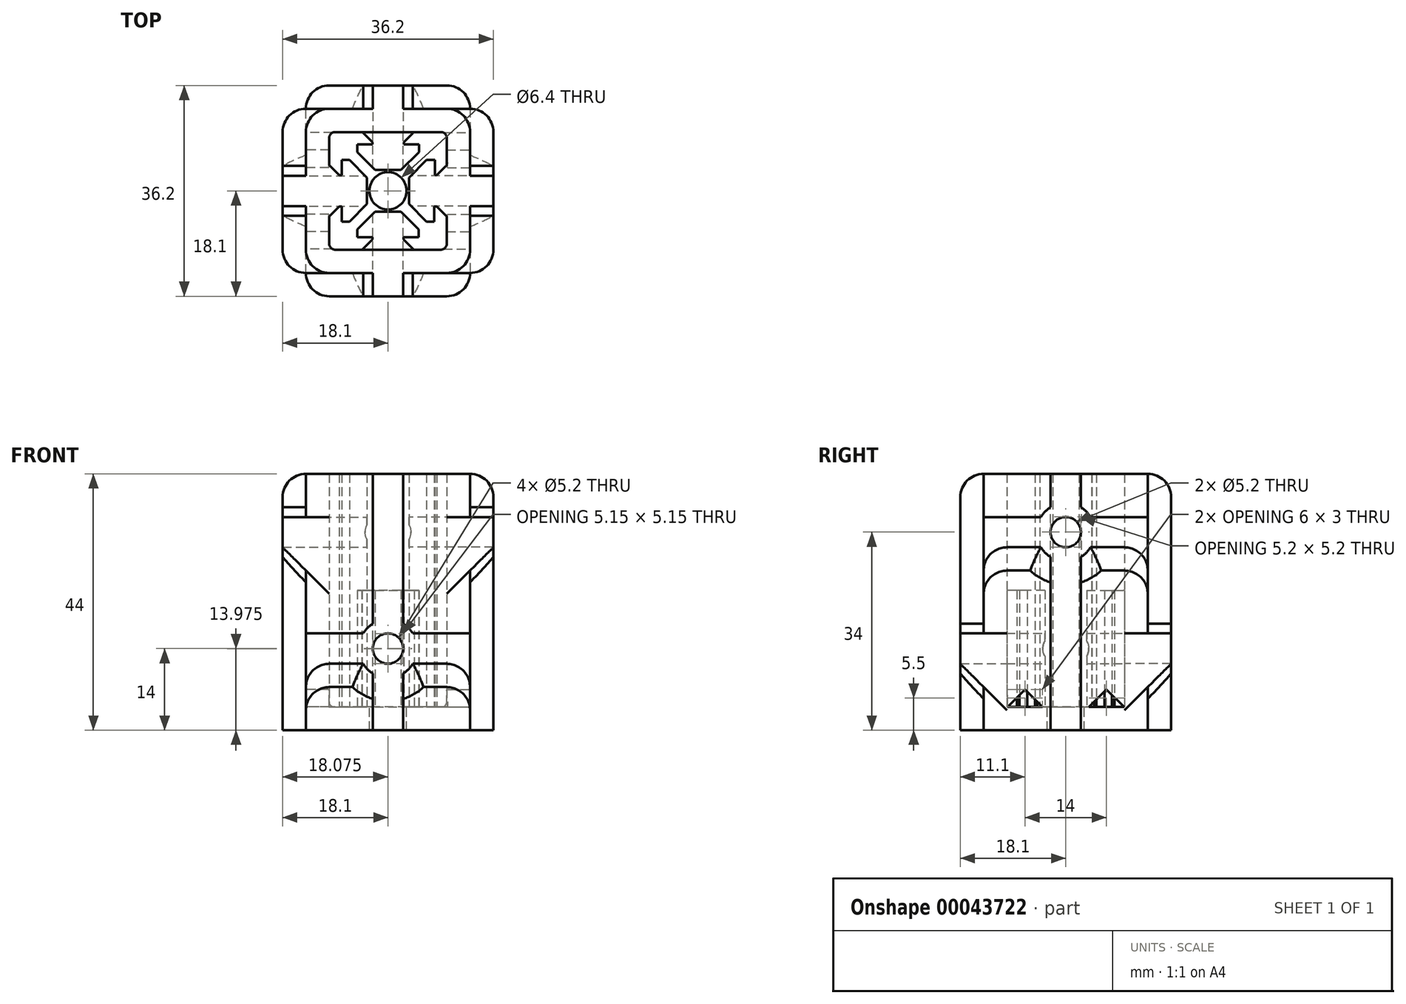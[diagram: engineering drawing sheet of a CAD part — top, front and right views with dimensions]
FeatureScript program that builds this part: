
annotation { "Feature Type Name" : "Feature", "Feature Type Description" : "" }
export const myFeature = defineFeature(function(context is Context, id is Id, definition is map)
    precondition{}
    {
        {
            var Q0;
            Q0=qCreatedBy(makeId("Top.planeOp"),FACE);
            var sketch = newSketch(context, id + "F0", { "sketchPlane" : qUnion([Q0])});
            skLineSegment(sketch, "E0.rect.bottom", {"start": v(10.1, -10.1) * mm, "end": v(-10.1, -10.1) * mm});
            skLineSegment(sketch, "E0.rect.top", {"start": v(10.1, 10.1) * mm, "end": v(-10.1, 10.1) * mm, "construction": true});
            skLineSegment(sketch, "E0.rect.left", {"start": v(10.1, -10.1) * mm, "end": v(10.1, 10.1) * mm, "construction": true});
            skLineSegment(sketch, "E0.rect.right", {"start": v(-10.1, -10.1) * mm, "end": v(-10.1, 10.1) * mm});
            skPoint(sketch, "E0.rect.middle", {"position": v(0, 0) * mm});
            skLineSegment(sketch, "E1.0", {"start": v(14.1, -14.1) * mm, "end": v(14.1, 14.1) * mm, "construction": true});
            skLineSegment(sketch, "E1.1", {"start": v(14.1, -14.1) * mm, "end": v(-14.1, -14.1) * mm});
            skLineSegment(sketch, "E1.2", {"start": v(-14.1, -14.1) * mm, "end": v(-14.1, 14.1) * mm});
            skLineSegment(sketch, "E1.3", {"start": v(14.1, 14.1) * mm, "end": v(-14.1, 14.1) * mm, "construction": true});
            skCircle(sketch, "E2", {"center": v(0, 0) * mm, "radius": 3.2 * mm});
            skLineSegment(sketch, "E3", {"start": v(-14.1, 14.1) * mm, "end": v(-2.26, 2.26) * mm});
            skLineSegment(sketch, "E4", {"start": v(2.26, -2.26) * mm, "end": v(14.1, -14.1) * mm});
            skSolve(sketch);
        }
        {
            var Q0;
            {var subQ5=sQuery(id+"F0.wireOp",EDGE,"E0.rect.right");Q0=makeQuery(id+"F0.imprint","IMPRINT",FACE,{"disambiguationData":[TD([[makeQuery(id+"F0.imprint","IMPRINT",EDGE,{"derivedFrom":subQ5}),1.0]])]});}
            extrude(context, id + "F1", {"entities" : qUnion([Q0]), "depth" : 40 * mm});
        }
        {
            var Q0;
            {var subQ3=sQuery(id+"F0.wireOp",EDGE,"E0.rect.bottom");Q0=makeQuery(id+"F0.imprint","IMPRINT",FACE,{"disambiguationData":[TD([[makeQuery(id+"F0.imprint","IMPRINT",EDGE,{"derivedFrom":subQ3}),1.0]])]});}
            var Q1;
            {var subQ0=sQuery(id+"F0.wireOp",EDGE,"E0.rect.bottom");Q1=makeQuery(id+"F0.imprint","IMPRINT",FACE,{"disambiguationData":[TD([[makeQuery(id+"F0.imprint","IMPRINT",EDGE,{"derivedFrom":subQ0}),-1.0]])]});}
            extrude(context, id + "F2", {"entities" : qUnion([Q0, Q1]), "operationType" : NewBodyOperationType.ADD, "oppositeDirection" : true, "depth" : 4 * mm});
        }
        {
            var Q0;
            Q0=qCreatedBy(makeId("Front.planeOp"),FACE);
            var sketch = newSketch(context, id + "F3", { "sketchPlane" : qUnion([Q0])});
            skCircle(sketch, "E5", {"center": v(0, 10) * mm, "radius": 2.6 * mm});
            skSolve(sketch);
        }
        {
            var Q0;
            Q0=makeQuery(id+"F3.imprint","IMPRINT",FACE,{"disambiguationData":[TD([[makeQuery(id+"F3.imprint","IMPRINT",EDGE,{"derivedFrom":sQuery(id+"F3.wireOp",EDGE,"E5")}),1.0]])]});
            extrude(context, id + "F4", {"entities" : qUnion([Q0]), "operationType" : NewBodyOperationType.REMOVE, "depth" : 25 * mm});
        }
        {
            var Q0;
            Q0=makeQuery(id+"F3.imprint","IMPRINT",FACE,{"disambiguationData":[TD([[makeQuery(id+"F3.imprint","IMPRINT",EDGE,{"derivedFrom":sQuery(id+"F3.wireOp",EDGE,"E5")}),-1.0]])]});
            var Q1;
            Q1=makeQuery(id+"F3.imprint","IMPRINT",FACE,{"disambiguationData":[TD([[makeQuery(id+"F3.imprint","IMPRINT",EDGE,{"derivedFrom":sQuery(id+"F3.wireOp",EDGE,"E5")}),1.0]])]});
            extrude(context, id + "F5", {"entities" : qUnion([Q0, Q1]), "operationType" : NewBodyOperationType.REMOVE, "oppositeDirection" : true, "depth" : 25 * mm});
        }
        {
            var Q0;
            Q0=qCreatedBy(makeId("Right.planeOp"),FACE);
            var sketch = newSketch(context, id + "F6", { "sketchPlane" : qUnion([Q0])});
            skCircle(sketch, "E6", {"center": v(0, 30) * mm, "radius": 2.6 * mm});
            skLineSegment(sketch, "E7", {"start": v(-10, 0) * mm, "end": v(-4, 0) * mm});
            skLineSegment(sketch, "E8", {"start": v(-4, 0) * mm, "end": v(-7, 3) * mm});
            skLineSegment(sketch, "E9", {"start": v(-7, 3) * mm, "end": v(-10, 0) * mm});
            skLineSegment(sketch, "E10", {"start": v(0, 0) * mm, "end": v(0, 30) * mm, "construction": true});
            skLineSegment(sketch, "E11.MirrorCS", {"start": v(10, 0) * mm, "end": v(4, 0) * mm});
            skLineSegment(sketch, "E12.MirrorCS", {"start": v(4, 0) * mm, "end": v(7, 3) * mm});
            skLineSegment(sketch, "E13.MirrorCS", {"start": v(7, 3) * mm, "end": v(10, 0) * mm});
            skSolve(sketch);
        }
        {
            var Q0;
            Q0=makeQuery(id+"F6.imprint","IMPRINT",FACE,{"disambiguationData":[TD([[makeQuery(id+"F6.imprint","IMPRINT",EDGE,{"derivedFrom":sQuery(id+"F6.wireOp",EDGE,"E6")}),1.0]])]});
            var Q1;
            Q1=makeQuery(id+"F6.imprint","IMPRINT",FACE,{"disambiguationData":[TD([[makeQuery(id+"F6.imprint","IMPRINT",EDGE,{"derivedFrom":sQuery(id+"F6.wireOp",EDGE,"f3287db6-100c-4814-bab7-777f2fd4f9ab")}),1.0]])]});
            extrude(context, id + "F7", {"entities" : qUnion([Q0, Q1]), "operationType" : NewBodyOperationType.REMOVE, "endBound" : BoundingType.SYMMETRIC, "oppositeDirection" : true, "depth" : 50 * mm});
        }
        {
            var Q0;
            Q0=makeQuery(id+"F6.imprint","IMPRINT",FACE,{"disambiguationData":[TD([[makeQuery(id+"F6.imprint","IMPRINT",EDGE,{"derivedFrom":sQuery(id+"F6.wireOp",EDGE,"E11.MirrorCS")}),-1.0]])]});
            var Q1;
            Q1=makeQuery(id+"F6.imprint","IMPRINT",FACE,{"disambiguationData":[TD([[makeQuery(id+"F6.imprint","IMPRINT",EDGE,{"derivedFrom":sQuery(id+"F6.wireOp",EDGE,"E7")}),1.0]])]});
            extrude(context, id + "F8", {"entities" : qUnion([Q0, Q1]), "operationType" : NewBodyOperationType.REMOVE, "endBound" : BoundingType.SYMMETRIC, "depth" : 50 * mm});
        }
        {
            var Q0;
            {var subQ0=sQuery(id+"F0.wireOp",EDGE,"E1.1");Q0=makeQuery(id+"F2.boolean.opBoolean","MERGE",FACE,{"derivedFrom":[makeQuery(id+"F9Dm1DlvACU9APN_1.boolean.opBoolean","MERGE",FACE,{"derivedFrom":[makeQuery(id+"F1.opExtrude","SWEPT_FACE",FACE,{"disambiguationData":[OSD([subQ0])]}),makeQuery(id+"F9Dm1DlvACU9APN_1.opExtrude","SWEPT_FACE",FACE,{"disambiguationData":[OSD([subQ0])]})]}),makeQuery(id+"F2.opExtrude","SWEPT_FACE",FACE,{"disambiguationData":[OSD([subQ0])]})]});}
            var sketch = newSketch(context, id + "F9", { "sketchPlane" : qUnion([Q0])});
            skArc(sketch, "E14", {"start": v(-4.27, 7.4) * mm, "mid": v(-3.54, 6.46) * mm, "end": v(-2.6, 5.73) * mm});
            skLineSegment(sketch, "E15.rect.bottom", {"start": v(2.6, 40) * mm, "end": v(-2.6, 40) * mm});
            skLineSegment(sketch, "E15.rect.left", {"start": v(2.6, 40) * mm, "end": v(2.6, 14.27) * mm});
            skLineSegment(sketch, "E15.rect.right", {"start": v(-2.6, 40) * mm, "end": v(-2.6, 14.27) * mm});
            skLineSegment(sketch, "E16.rect.bottom", {"start": v(14.1, 12.6) * mm, "end": v(4.27, 12.6) * mm});
            skLineSegment(sketch, "E16.rect.top", {"start": v(14.1, 7.4) * mm, "end": v(4.27, 7.4) * mm});
            skLineSegment(sketch, "E16.rect.left", {"start": v(14.1, 12.6) * mm, "end": v(14.1, 7.4) * mm});
            skLineSegment(sketch, "E16.rect.right", {"start": v(-14.1, 12.6) * mm, "end": v(-14.1, 7.4) * mm});
            skLineSegment(sketch, "E17.0", {"start": v(2.6, -4) * mm, "end": v(-2.6, -4) * mm});
            skLineSegment(sketch, "E18.trimOffspring", {"start": v(-2.6, 5.73) * mm, "end": v(-2.6, -4) * mm});
            skLineSegment(sketch, "E19.trimOffspring", {"start": v(-4.27, 7.4) * mm, "end": v(-14.1, 7.4) * mm});
            skLineSegment(sketch, "E20.trimOffspring", {"start": v(-4.27, 12.6) * mm, "end": v(-14.1, 12.6) * mm});
            skLineSegment(sketch, "E21.trimOffspring", {"start": v(2.6, 5.73) * mm, "end": v(2.6, -4) * mm});
            skArc(sketch, "E22.trimOffspring", {"start": v(-2.6, 14.27) * mm, "mid": v(-3.54, 13.54) * mm, "end": v(-4.27, 12.6) * mm});
            skArc(sketch, "E23.trimOffspring", {"start": v(4.27, 12.6) * mm, "mid": v(3.54, 13.54) * mm, "end": v(2.6, 14.27) * mm});
            skArc(sketch, "E24.trimOffspring", {"start": v(2.6, 5.73) * mm, "mid": v(3.54, 6.46) * mm, "end": v(4.27, 7.4) * mm});
            skSolve(sketch);
        }
        {
            var Q0;
            {var subQ0=sQuery(id+"F0.wireOp",EDGE,"E1.2");Q0=makeQuery(id+"F2.boolean.opBoolean","MERGE",FACE,{"derivedFrom":[makeQuery(id+"F1.opExtrude","SWEPT_FACE",FACE,{"disambiguationData":[OSD([subQ0])]}),makeQuery(id+"F2.opExtrude","SWEPT_FACE",FACE,{"disambiguationData":[OSD([subQ0])]})]});}
            var sketch = newSketch(context, id + "F10", { "sketchPlane" : qUnion([Q0])});
            skArc(sketch, "E25", {"start": v(-4.27, 27.4) * mm, "mid": v(-3.54, 26.46) * mm, "end": v(-2.6, 25.73) * mm});
            skLineSegment(sketch, "E26.rect.bottom", {"start": v(2.6, -4) * mm, "end": v(-2.6, -4) * mm});
            skLineSegment(sketch, "E26.rect.left", {"start": v(2.6, -4) * mm, "end": v(2.6, 25.73) * mm});
            skLineSegment(sketch, "E26.rect.right", {"start": v(-2.6, -4) * mm, "end": v(-2.6, 25.73) * mm});
            skLineSegment(sketch, "E27.0", {"start": v(2.6, 40) * mm, "end": v(-2.6, 40) * mm});
            skLineSegment(sketch, "E28.rect.bottom", {"start": v(14.1, 32.6) * mm, "end": v(4.27, 32.6) * mm});
            skLineSegment(sketch, "E28.rect.top", {"start": v(14.1, 27.4) * mm, "end": v(4.27, 27.4) * mm});
            skLineSegment(sketch, "E28.rect.left", {"start": v(14.1, 32.6) * mm, "end": v(14.1, 27.4) * mm});
            skLineSegment(sketch, "E28.rect.right", {"start": v(-14.1, 32.6) * mm, "end": v(-14.1, 27.4) * mm});
            skLineSegment(sketch, "E29.trimOffspring", {"start": v(-4.27, 32.6) * mm, "end": v(-14.1, 32.6) * mm});
            skLineSegment(sketch, "E30.trimOffspring", {"start": v(-2.6, 34.27) * mm, "end": v(-2.6, 40) * mm});
            skLineSegment(sketch, "E31.trimOffspring", {"start": v(2.6, 34.27) * mm, "end": v(2.6, 40) * mm});
            skLineSegment(sketch, "E32.trimOffspring", {"start": v(-4.27, 27.4) * mm, "end": v(-14.1, 27.4) * mm});
            skArc(sketch, "E33.trimOffspring", {"start": v(-2.6, 34.27) * mm, "mid": v(-3.54, 33.54) * mm, "end": v(-4.27, 32.6) * mm});
            skArc(sketch, "E34.trimOffspring", {"start": v(4.27, 32.6) * mm, "mid": v(3.54, 33.54) * mm, "end": v(2.6, 34.27) * mm});
            skArc(sketch, "E35.trimOffspring", {"start": v(2.6, 25.73) * mm, "mid": v(3.54, 26.46) * mm, "end": v(4.27, 27.4) * mm});
            skSolve(sketch);
        }
        {
            var Q0;
            Q0=makeQuery(id+"F9.imprint","IMPRINT",FACE,{"disambiguationData":[TD([[makeQuery(id+"F9.imprint","IMPRINT",EDGE,{"derivedFrom":sQuery(id+"F9.wireOp",EDGE,"E14")}),1.0]])]});
            extrude(context, id + "F11", {"entities" : qUnion([Q0]), "operationType" : NewBodyOperationType.ADD, "depth" : 4 * mm});
        }
        {
            var Q0;
            Q0=makeQuery(id+"F11.opExtrude","CAP_EDGE",EDGE,{"disambiguationData":[OSD([sQuery(id+"F9.wireOp",EDGE,"E14")])],"isStart":true});
            var Q1;
            Q1=makeQuery(id+"F11.opExtrude","CAP_EDGE",EDGE,{"disambiguationData":[OSD([sQuery(id+"F9.wireOp",EDGE,"E24.trimOffspring")])],"isStart":true});
            var Q2;
            Q2=makeQuery(id+"F11.opExtrude","CAP_EDGE",EDGE,{"disambiguationData":[OSD([sQuery(id+"F9.wireOp",EDGE,"E16.rect.top")])],"isStart":true});
            var Q3;
            Q3=makeQuery(id+"F11.opExtrude","CAP_EDGE",EDGE,{"disambiguationData":[OSD([sQuery(id+"F9.wireOp",EDGE,"E19.trimOffspring")])],"isStart":true});
            chamfer(context, id + "F12", {"entities" : qUnion([Q0, Q1, Q2, Q3]), "width" : 4 * mm, "tangentPropagation" : true});
        }
        {
            var Q0;
            Q0=makeQuery(id+"F10.imprint","IMPRINT",FACE,{"disambiguationData":[TD([[makeQuery(id+"F10.imprint","IMPRINT",EDGE,{"derivedFrom":sQuery(id+"F10.wireOp",EDGE,"E25")}),1.0]])]});
            extrude(context, id + "F13", {"entities" : qUnion([Q0]), "operationType" : NewBodyOperationType.ADD, "depth" : 4 * mm});
        }
        {
            var Q0;
            Q0=makeQuery(id+"F13.opExtrude","CAP_EDGE",EDGE,{"disambiguationData":[OSD([sQuery(id+"F10.wireOp",EDGE,"E25")])],"isStart":true});
            var Q1;
            Q1=makeQuery(id+"F13.opExtrude","CAP_EDGE",EDGE,{"disambiguationData":[OSD([sQuery(id+"F10.wireOp",EDGE,"E32.trimOffspring")])],"isStart":true});
            var Q2;
            Q2=makeQuery(id+"F13.opExtrude","CAP_EDGE",EDGE,{"disambiguationData":[OSD([sQuery(id+"F10.wireOp",EDGE,"E35.trimOffspring")])],"isStart":true});
            var Q3;
            Q3=makeQuery(id+"F13.opExtrude","CAP_EDGE",EDGE,{"disambiguationData":[OSD([sQuery(id+"F10.wireOp",EDGE,"E28.rect.top")])],"isStart":true});
            chamfer(context, id + "F14", {"entities" : qUnion([Q0, Q1, Q2, Q3]), "width" : 4 * mm, "tangentPropagation" : true});
        }
        {
            var Q0;
            Q0=qCreatedBy(makeId("Top.planeOp"),FACE);
            var sketch = newSketch(context, id + "F15", { "sketchPlane" : qUnion([Q0])});
            skLineSegment(sketch, "E36", {"start": v(-8.2, -8.2) * mm, "end": v(-6.57, -8.2) * mm});
            skLineSegment(sketch, "E37", {"start": v(-8.2, -6.57) * mm, "end": v(-8.2, -8.2) * mm});
            skLineSegment(sketch, "E38", {"start": v(-7.66, -6.57) * mm, "end": v(-8.2, -6.57) * mm});
            skLineSegment(sketch, "E39", {"start": v(-6.57, -7.66) * mm, "end": v(-7.66, -6.57) * mm});
            skLineSegment(sketch, "E40", {"start": v(-6.57, -8.2) * mm, "end": v(-6.57, -7.66) * mm});
            skLineSegment(sketch, "E41", {"start": v(7.66, -6.57) * mm, "end": v(6.57, -7.66) * mm});
            skLineSegment(sketch, "E42", {"start": v(8.2, -6.57) * mm, "end": v(7.66, -6.57) * mm});
            skLineSegment(sketch, "E43", {"start": v(8.2, -8.2) * mm, "end": v(8.2, -6.57) * mm});
            skLineSegment(sketch, "E44", {"start": v(6.57, -8.2) * mm, "end": v(8.2, -8.2) * mm});
            skLineSegment(sketch, "E45", {"start": v(6.57, -7.66) * mm, "end": v(6.57, -8.2) * mm});
            skCircle(sketch, "E46", {"center": v(0, 0) * mm, "radius": 2.1 * mm});
            skLineSegment(sketch, "E47", {"start": v(8.2, 8.2) * mm, "end": v(6.57, 8.2) * mm});
            skLineSegment(sketch, "E48", {"start": v(8.2, 6.57) * mm, "end": v(8.2, 8.2) * mm});
            skLineSegment(sketch, "E49", {"start": v(7.66, 6.57) * mm, "end": v(8.2, 6.57) * mm});
            skLineSegment(sketch, "E50", {"start": v(6.57, 7.66) * mm, "end": v(7.66, 6.57) * mm});
            skLineSegment(sketch, "E51", {"start": v(6.57, 8.2) * mm, "end": v(6.57, 7.66) * mm});
            skLineSegment(sketch, "E52", {"start": v(-7.66, 6.57) * mm, "end": v(-6.57, 7.66) * mm});
            skLineSegment(sketch, "E53", {"start": v(-8.2, 6.57) * mm, "end": v(-7.66, 6.57) * mm});
            skLineSegment(sketch, "E54", {"start": v(-8.2, 8.2) * mm, "end": v(-8.2, 6.57) * mm});
            skLineSegment(sketch, "E55", {"start": v(-6.57, 8.2) * mm, "end": v(-8.2, 8.2) * mm});
            skLineSegment(sketch, "E56", {"start": v(-6.57, 7.66) * mm, "end": v(-6.57, 8.2) * mm});
            skLineSegment(sketch, "E57", {"start": v(-6.55, 5.5) * mm, "end": v(-3.39, 2.33) * mm});
            skLineSegment(sketch, "E58", {"start": v(-3.4, 2.35) * mm, "end": v(-3.4, -2.33) * mm});
            skLineSegment(sketch, "E59", {"start": v(-3.39, -2.32) * mm, "end": v(-6.55, -5.48) * mm});
            skLineSegment(sketch, "E60", {"start": v(-6.53, -5.47) * mm, "end": v(-8.17, -5.47) * mm});
            skLineSegment(sketch, "E61", {"start": v(-8.16, -5.5) * mm, "end": v(-8.16, -2.88) * mm});
            skLineSegment(sketch, "E62", {"start": v(-8.17, -2.86) * mm, "end": v(-8.28, -2.86) * mm});
            skLineSegment(sketch, "E63", {"start": v(-8.3, -2.87) * mm, "end": v(-9.76, -4.33) * mm});
            skArc(sketch, "E64", {"start": v(-9.76, -4.33) * mm, "mid": v(-9.93, -4.58) * mm, "end": v(-9.99, -4.89) * mm});
            skLineSegment(sketch, "E65", {"start": v(-9.99, -4.89) * mm, "end": v(-9.99, -8.48) * mm});
            skArc(sketch, "E66", {"start": v(-9.99, -8.48) * mm, "mid": v(-9.55, -9.54) * mm, "end": v(-8.49, -9.98) * mm});
            skLineSegment(sketch, "E67", {"start": v(-8.49, -9.98) * mm, "end": v(-4.9, -9.98) * mm});
            skArc(sketch, "E68", {"start": v(-4.9, -9.98) * mm, "mid": v(-4.6, -9.92) * mm, "end": v(-4.34, -9.75) * mm});
            skLineSegment(sketch, "E69", {"start": v(-4.34, -9.75) * mm, "end": v(-2.88, -8.29) * mm});
            skLineSegment(sketch, "E70", {"start": v(-2.87, -8.28) * mm, "end": v(-2.87, -8.17) * mm});
            skLineSegment(sketch, "E71", {"start": v(-2.9, -8.15) * mm, "end": v(-5.5, -8.15) * mm});
            skLineSegment(sketch, "E72", {"start": v(-5.48, -8.17) * mm, "end": v(-5.48, -6.53) * mm});
            skLineSegment(sketch, "E73", {"start": v(-5.49, -6.54) * mm, "end": v(-2.33, -3.38) * mm});
            skLineSegment(sketch, "E74", {"start": v(-2.34, -3.38) * mm, "end": v(2.34, -3.38) * mm});
            skLineSegment(sketch, "E75", {"start": v(2.33, -3.38) * mm, "end": v(5.49, -6.54) * mm});
            skLineSegment(sketch, "E76", {"start": v(5.48, -6.53) * mm, "end": v(5.48, -8.17) * mm});
            skLineSegment(sketch, "E77", {"start": v(5.5, -8.15) * mm, "end": v(2.89, -8.15) * mm});
            skLineSegment(sketch, "E78", {"start": v(2.87, -8.17) * mm, "end": v(2.87, -8.28) * mm});
            skLineSegment(sketch, "E79", {"start": v(2.88, -8.29) * mm, "end": v(4.34, -9.75) * mm});
            skArc(sketch, "E80", {"start": v(4.34, -9.75) * mm, "mid": v(4.6, -9.92) * mm, "end": v(4.9, -9.98) * mm});
            skLineSegment(sketch, "E81", {"start": v(4.9, -9.98) * mm, "end": v(8.49, -9.98) * mm});
            skArc(sketch, "E82", {"start": v(8.49, -9.98) * mm, "mid": v(9.55, -9.54) * mm, "end": v(9.99, -8.48) * mm});
            skLineSegment(sketch, "E83", {"start": v(9.99, -8.48) * mm, "end": v(9.99, -4.89) * mm});
            skArc(sketch, "E84", {"start": v(9.99, -4.89) * mm, "mid": v(9.93, -4.58) * mm, "end": v(9.76, -4.33) * mm});
            skLineSegment(sketch, "E85", {"start": v(9.76, -4.33) * mm, "end": v(8.3, -2.87) * mm});
            skLineSegment(sketch, "E86", {"start": v(8.28, -2.86) * mm, "end": v(8.17, -2.86) * mm});
            skLineSegment(sketch, "E87", {"start": v(8.16, -2.88) * mm, "end": v(8.16, -5.5) * mm});
            skLineSegment(sketch, "E88", {"start": v(8.17, -5.47) * mm, "end": v(6.53, -5.47) * mm});
            skLineSegment(sketch, "E89", {"start": v(6.55, -5.48) * mm, "end": v(3.39, -2.32) * mm});
            skLineSegment(sketch, "E90", {"start": v(3.4, -2.33) * mm, "end": v(3.4, 2.35) * mm});
            skLineSegment(sketch, "E91", {"start": v(3.39, 2.33) * mm, "end": v(6.55, 5.5) * mm});
            skLineSegment(sketch, "E92", {"start": v(6.53, 5.49) * mm, "end": v(8.17, 5.49) * mm});
            skLineSegment(sketch, "E93", {"start": v(8.24, 5.5) * mm, "end": v(8.24, 2.9) * mm});
            skLineSegment(sketch, "E94", {"start": v(8.21, 2.88) * mm, "end": v(8.32, 2.88) * mm});
            skLineSegment(sketch, "E95", {"start": v(8.33, 2.88) * mm, "end": v(9.8, 4.34) * mm});
            skArc(sketch, "E96", {"start": v(9.8, 4.34) * mm, "mid": v(9.96, 4.6) * mm, "end": v(10.02, 4.9) * mm});
            skLineSegment(sketch, "E97", {"start": v(10.02, 4.9) * mm, "end": v(10.02, 8.5) * mm});
            skArc(sketch, "E98", {"start": v(10.02, 8.5) * mm, "mid": v(9.58, 9.56) * mm, "end": v(8.52, 10) * mm});
            skLineSegment(sketch, "E99", {"start": v(8.52, 10) * mm, "end": v(4.93, 10) * mm});
            skArc(sketch, "E100", {"start": v(4.93, 10) * mm, "mid": v(4.63, 9.93) * mm, "end": v(4.37, 9.76) * mm});
            skLineSegment(sketch, "E101", {"start": v(4.37, 9.76) * mm, "end": v(2.91, 8.3) * mm});
            skLineSegment(sketch, "E102", {"start": v(2.9, 8.3) * mm, "end": v(2.9, 8.18) * mm});
            skLineSegment(sketch, "E103", {"start": v(2.93, 8.16) * mm, "end": v(5.54, 8.16) * mm});
            skLineSegment(sketch, "E104", {"start": v(5.52, 8.18) * mm, "end": v(5.52, 6.54) * mm});
            skLineSegment(sketch, "E105", {"start": v(5.51, 6.54) * mm, "end": v(2.33, 3.4) * mm});
            skLineSegment(sketch, "E106", {"start": v(2.34, 3.4) * mm, "end": v(-2.34, 3.4) * mm});
            skLineSegment(sketch, "E107", {"start": v(-2.33, 3.4) * mm, "end": v(-5.49, 6.56) * mm});
            skLineSegment(sketch, "E108", {"start": v(-5.48, 6.54) * mm, "end": v(-5.48, 8.18) * mm});
            skLineSegment(sketch, "E109", {"start": v(-5.5, 8.16) * mm, "end": v(-2.9, 8.16) * mm});
            skLineSegment(sketch, "E110", {"start": v(-2.87, 8.18) * mm, "end": v(-2.87, 8.3) * mm});
            skLineSegment(sketch, "E111", {"start": v(-2.88, 8.3) * mm, "end": v(-4.34, 9.76) * mm});
            skArc(sketch, "E112", {"start": v(-4.34, 9.76) * mm, "mid": v(-4.6, 9.93) * mm, "end": v(-4.9, 10) * mm});
            skLineSegment(sketch, "E113", {"start": v(-4.9, 10) * mm, "end": v(-8.49, 10) * mm});
            skArc(sketch, "E114", {"start": v(-8.49, 10) * mm, "mid": v(-9.55, 9.56) * mm, "end": v(-9.99, 8.5) * mm});
            skLineSegment(sketch, "E115", {"start": v(-9.99, 8.5) * mm, "end": v(-9.99, 4.9) * mm});
            skArc(sketch, "E116", {"start": v(-9.99, 4.9) * mm, "mid": v(-9.93, 4.6) * mm, "end": v(-9.76, 4.34) * mm});
            skLineSegment(sketch, "E117", {"start": v(-9.76, 4.34) * mm, "end": v(-8.3, 2.88) * mm});
            skLineSegment(sketch, "E118", {"start": v(-8.28, 2.88) * mm, "end": v(-8.17, 2.88) * mm});
            skLineSegment(sketch, "E119", {"start": v(-8.16, 2.9) * mm, "end": v(-8.16, 5.5) * mm});
            skLineSegment(sketch, "E120", {"start": v(-8.17, 5.49) * mm, "end": v(-6.53, 5.49) * mm});
            skLineSegment(sketch, "E121.0", {"start": v(2.25, 3.6) * mm, "end": v(-2.25, 3.6) * mm});
            skLineSegment(sketch, "E121.1", {"start": v(5.32, 6.63) * mm, "end": v(2.25, 3.6) * mm});
            skLineSegment(sketch, "E121.2", {"start": v(5.32, 7.96) * mm, "end": v(5.32, 6.63) * mm});
            skLineSegment(sketch, "E121.3", {"start": v(2.7, 7.96) * mm, "end": v(5.32, 7.96) * mm});
            skLineSegment(sketch, "E121.4", {"start": v(2.7, 8.38) * mm, "end": v(2.7, 7.96) * mm});
            skLineSegment(sketch, "E121.5", {"start": v(4.23, 9.9) * mm, "end": v(2.7, 8.38) * mm});
            skArc(sketch, "E121.6", {"start": v(4.93, 10.2) * mm, "mid": v(4.55, 10.12) * mm, "end": v(4.23, 9.9) * mm});
            skLineSegment(sketch, "E121.7", {"start": v(8.52, 10.2) * mm, "end": v(4.93, 10.2) * mm});
            skArc(sketch, "E121.8", {"start": v(10.22, 8.5) * mm, "mid": v(9.73, 9.7) * mm, "end": v(8.52, 10.2) * mm});
            skLineSegment(sketch, "E121.9", {"start": v(10.22, 4.9) * mm, "end": v(10.22, 8.5) * mm});
            skArc(sketch, "E121.10", {"start": v(9.93, 4.2) * mm, "mid": v(10.15, 4.52) * mm, "end": v(10.22, 4.9) * mm});
            skLineSegment(sketch, "E121.11", {"start": v(8.41, 2.68) * mm, "end": v(9.93, 4.2) * mm});
            skLineSegment(sketch, "E121.12", {"start": v(8.04, 2.68) * mm, "end": v(8.41, 2.68) * mm});
            skLineSegment(sketch, "E121.13", {"start": v(8.04, 5.29) * mm, "end": v(8.04, 2.68) * mm});
            skLineSegment(sketch, "E121.14", {"start": v(6.63, 5.29) * mm, "end": v(8.04, 5.29) * mm});
            skLineSegment(sketch, "E121.15", {"start": v(3.6, 2.26) * mm, "end": v(6.63, 5.29) * mm});
            skLineSegment(sketch, "E121.16", {"start": v(3.6, -2.24) * mm, "end": v(3.6, 2.26) * mm});
            skLineSegment(sketch, "E121.17", {"start": v(6.63, -5.27) * mm, "end": v(3.6, -2.24) * mm});
            skArc(sketch, "E121.18", {"start": v(-9.9, -4.19) * mm, "mid": v(-10.11, -4.5) * mm, "end": v(-10.19, -4.89) * mm});
            skLineSegment(sketch, "E121.19", {"start": v(-8.37, -2.66) * mm, "end": v(-9.9, -4.19) * mm});
            skLineSegment(sketch, "E121.20", {"start": v(-7.96, -2.66) * mm, "end": v(-8.37, -2.66) * mm});
            skLineSegment(sketch, "E121.21", {"start": v(-7.96, -5.27) * mm, "end": v(-7.96, -2.66) * mm});
            skLineSegment(sketch, "E121.22", {"start": v(-6.63, -5.27) * mm, "end": v(-7.96, -5.27) * mm});
            skLineSegment(sketch, "E121.23", {"start": v(-3.6, -2.24) * mm, "end": v(-6.63, -5.27) * mm});
            skLineSegment(sketch, "E121.24", {"start": v(-3.6, 2.26) * mm, "end": v(-3.6, -2.24) * mm});
            skLineSegment(sketch, "E121.25", {"start": v(-6.63, 5.29) * mm, "end": v(-3.6, 2.26) * mm});
            skLineSegment(sketch, "E121.26", {"start": v(-7.96, 5.29) * mm, "end": v(-6.63, 5.29) * mm});
            skLineSegment(sketch, "E121.27", {"start": v(-7.96, 2.68) * mm, "end": v(-7.96, 5.29) * mm});
            skLineSegment(sketch, "E121.28", {"start": v(-8.37, 2.68) * mm, "end": v(-7.96, 2.68) * mm});
            skLineSegment(sketch, "E121.29", {"start": v(-9.9, 4.2) * mm, "end": v(-8.37, 2.68) * mm});
            skLineSegment(sketch, "E121.30", {"start": v(-2.67, 7.96) * mm, "end": v(-2.67, 8.38) * mm});
            skLineSegment(sketch, "E121.31", {"start": v(-5.28, 7.96) * mm, "end": v(-2.67, 7.96) * mm});
            skLineSegment(sketch, "E121.32", {"start": v(-5.28, 6.63) * mm, "end": v(-5.28, 7.96) * mm});
            skLineSegment(sketch, "E121.33", {"start": v(-2.25, 3.6) * mm, "end": v(-5.28, 6.63) * mm});
            skLineSegment(sketch, "E121.34", {"start": v(-2.67, 8.38) * mm, "end": v(-4.2, 9.9) * mm});
            skArc(sketch, "E121.35", {"start": v(-4.2, 9.9) * mm, "mid": v(-4.52, 10.12) * mm, "end": v(-4.9, 10.2) * mm});
            skLineSegment(sketch, "E121.36", {"start": v(-4.9, 10.2) * mm, "end": v(-8.49, 10.2) * mm});
            skArc(sketch, "E121.37", {"start": v(-8.49, 10.2) * mm, "mid": v(-9.69, 9.7) * mm, "end": v(-10.19, 8.5) * mm});
            skLineSegment(sketch, "E121.38", {"start": v(-10.19, 8.5) * mm, "end": v(-10.19, 4.9) * mm});
            skArc(sketch, "E121.39", {"start": v(-10.19, 4.9) * mm, "mid": v(-10.11, 4.52) * mm, "end": v(-9.9, 4.2) * mm});
            skLineSegment(sketch, "E121.40", {"start": v(-10.19, -4.89) * mm, "end": v(-10.19, -8.48) * mm});
            skArc(sketch, "E121.41", {"start": v(-10.19, -8.48) * mm, "mid": v(-9.69, -9.68) * mm, "end": v(-8.49, -10.18) * mm});
            skLineSegment(sketch, "E121.42", {"start": v(-8.49, -10.18) * mm, "end": v(-4.9, -10.18) * mm});
            skArc(sketch, "E121.43", {"start": v(-4.9, -10.18) * mm, "mid": v(-4.52, -10.1) * mm, "end": v(-4.2, -9.89) * mm});
            skLineSegment(sketch, "E121.44", {"start": v(-4.2, -9.89) * mm, "end": v(-2.67, -8.37) * mm});
            skLineSegment(sketch, "E121.45", {"start": v(-2.67, -8.37) * mm, "end": v(-2.67, -7.95) * mm});
            skLineSegment(sketch, "E121.46", {"start": v(-2.67, -7.95) * mm, "end": v(-5.28, -7.95) * mm});
            skLineSegment(sketch, "E121.47", {"start": v(-5.28, -7.95) * mm, "end": v(-5.28, -6.62) * mm});
            skLineSegment(sketch, "E121.48", {"start": v(-5.28, -6.62) * mm, "end": v(-2.25, -3.58) * mm});
            skLineSegment(sketch, "E121.49", {"start": v(-2.25, -3.58) * mm, "end": v(2.25, -3.58) * mm});
            skLineSegment(sketch, "E121.50", {"start": v(2.25, -3.58) * mm, "end": v(5.28, -6.62) * mm});
            skLineSegment(sketch, "E121.51", {"start": v(5.28, -6.62) * mm, "end": v(5.28, -7.95) * mm});
            skLineSegment(sketch, "E121.52", {"start": v(5.28, -7.95) * mm, "end": v(2.67, -7.95) * mm});
            skLineSegment(sketch, "E121.53", {"start": v(2.67, -7.95) * mm, "end": v(2.67, -8.37) * mm});
            skLineSegment(sketch, "E121.54", {"start": v(2.67, -8.37) * mm, "end": v(4.2, -9.89) * mm});
            skArc(sketch, "E121.55", {"start": v(4.2, -9.89) * mm, "mid": v(4.52, -10.1) * mm, "end": v(4.9, -10.18) * mm});
            skLineSegment(sketch, "E121.56", {"start": v(4.9, -10.18) * mm, "end": v(8.49, -10.18) * mm});
            skArc(sketch, "E121.57", {"start": v(8.49, -10.18) * mm, "mid": v(9.69, -9.68) * mm, "end": v(10.19, -8.48) * mm});
            skLineSegment(sketch, "E121.58", {"start": v(10.19, -8.48) * mm, "end": v(10.19, -4.89) * mm});
            skArc(sketch, "E121.59", {"start": v(10.19, -4.89) * mm, "mid": v(10.11, -4.5) * mm, "end": v(9.9, -4.19) * mm});
            skLineSegment(sketch, "E121.60", {"start": v(9.9, -4.19) * mm, "end": v(8.37, -2.66) * mm});
            skLineSegment(sketch, "E121.61", {"start": v(8.37, -2.66) * mm, "end": v(7.96, -2.66) * mm});
            skLineSegment(sketch, "E121.62", {"start": v(7.96, -2.66) * mm, "end": v(7.96, -5.27) * mm});
            skLineSegment(sketch, "E121.63", {"start": v(7.96, -5.27) * mm, "end": v(6.63, -5.27) * mm});
            skLineSegment(sketch, "E122", {"start": v(-4.9, 10.2) * mm, "end": v(4.93, 10.2) * mm});
            skLineSegment(sketch, "E123", {"start": v(-10.19, -4.89) * mm, "end": v(-10.19, 4.9) * mm});
            skLineSegment(sketch, "E124", {"start": v(-4.9, -10.18) * mm, "end": v(4.9, -10.18) * mm});
            skLineSegment(sketch, "E125", {"start": v(10.19, -4.89) * mm, "end": v(10.22, 4.9) * mm});
            skSolve(sketch);
        }
        {
            var Q0;
            Q0=makeQuery(id+"F1.opExtrude","SWEPT_BODY",BODY,{"disambiguationData":[OSD([sQuery(id+"F0.wireOp",EDGE,"E0.rect.bottom"),sQuery(id+"F0.wireOp",EDGE,"E0.rect.right"),sQuery(id+"F0.wireOp",EDGE,"E1.1"),sQuery(id+"F0.wireOp",EDGE,"E1.2"),sQuery(id+"F0.wireOp",EDGE,"E3"),sQuery(id+"F0.wireOp",EDGE,"E4")])]});
            var Q1;
            {var subQ0=sQuery(id+"F0.wireOp",EDGE,"E3");Q1=makeQuery(id+"F2.boolean.opBoolean","MERGE",FACE,{"derivedFrom":[makeQuery(id+"F1.opExtrude","SWEPT_FACE",FACE,{"disambiguationData":[OSD([subQ0])]}),makeQuery(id+"F2.opExtrude","SWEPT_FACE",FACE,{"disambiguationData":[OSD([subQ0])]})]});}
            mirror(context, id + "F16", {"entities" : qUnion([Q0]), "mirrorPlane" : qUnion([Q1])});
        }
        {
            var Q0;
            Q0=makeQuery(id+"F16.opPattern","COPY",VERTEX,{"derivedFrom":makeQuery(id+"F1.opExtrude","CAP_VERTEX",VERTEX,{"disambiguationData":[OSD([sQuery(id+"F0.wireOp",EDGE,"E1.1"),sQuery(id+"F0.wireOp",EDGE,"E1.2")])],"isStart":false}),"instanceName":"1"});
            var Q1;
            Q1=makeQuery(id+"F1.opExtrude","CAP_VERTEX",VERTEX,{"disambiguationData":[OSD([sQuery(id+"F0.wireOp",EDGE,"E1.1"),sQuery(id+"F0.wireOp",EDGE,"E1.2")])],"isStart":false});
            var Q2;
            Q2=makeQuery(id+"F2.opExtrude","CAP_VERTEX",VERTEX,{"disambiguationData":[OSD([sQuery(id+"F0.wireOp",EDGE,"E1.1"),sQuery(id+"F0.wireOp",EDGE,"E1.2")])],"isStart":false});
            cPlane(context, id + "F17", {"entities" : qUnion([Q0, Q1, Q2]), "cplaneType" : CPlaneType.THREE_POINT, "offset" : 0 * mm, "width" : 150 * mm, "height" : 150 * mm});
        }
        {
            var Q0;
            Q0=makeQuery(id+"F16.opPattern","COPY",BODY,{"derivedFrom":makeQuery(id+"F1.opExtrude","SWEPT_BODY",BODY,{"disambiguationData":[OSD([sQuery(id+"F0.wireOp",EDGE,"E0.rect.bottom"),sQuery(id+"F0.wireOp",EDGE,"E0.rect.right"),sQuery(id+"F0.wireOp",EDGE,"E1.1"),sQuery(id+"F0.wireOp",EDGE,"E1.2"),sQuery(id+"F0.wireOp",EDGE,"E3"),sQuery(id+"F0.wireOp",EDGE,"E4")])]}),"instanceName":"1"});
            var Q1;
            Q1=qCreatedBy(id+"F17.planeOp",FACE);
            mirror(context, id + "F18", {"entities" : qUnion([Q0]), "mirrorPlane" : qUnion([Q1])});
        }
        {
            var Q0;
            Q0=makeQuery(id+"F16.opPattern","COPY",BODY,{"derivedFrom":makeQuery(id+"F1.opExtrude","SWEPT_BODY",BODY,{"disambiguationData":[OSD([sQuery(id+"F0.wireOp",EDGE,"E0.rect.bottom"),sQuery(id+"F0.wireOp",EDGE,"E0.rect.right"),sQuery(id+"F0.wireOp",EDGE,"E1.1"),sQuery(id+"F0.wireOp",EDGE,"E1.2"),sQuery(id+"F0.wireOp",EDGE,"E3"),sQuery(id+"F0.wireOp",EDGE,"E4")])]}),"instanceName":"1"});
            deleteBodies(context, id + "F19", {"entities" : qUnion([Q0])});
        }
        {
            var Q0;
            Q0=makeQuery(id+"F1.opExtrude","SWEPT_BODY",BODY,{"disambiguationData":[OSD([sQuery(id+"F0.wireOp",EDGE,"E0.rect.bottom"),sQuery(id+"F0.wireOp",EDGE,"E0.rect.right"),sQuery(id+"F0.wireOp",EDGE,"E1.1"),sQuery(id+"F0.wireOp",EDGE,"E1.2"),sQuery(id+"F0.wireOp",EDGE,"E3"),sQuery(id+"F0.wireOp",EDGE,"E4")])]});
            var Q1;
            Q1=makeQuery(id+"F18.opPattern","COPY",BODY,{"derivedFrom":makeQuery(id+"F16.opPattern","COPY",BODY,{"derivedFrom":makeQuery(id+"F1.opExtrude","SWEPT_BODY",BODY,{"disambiguationData":[OSD([sQuery(id+"F0.wireOp",EDGE,"E0.rect.bottom"),sQuery(id+"F0.wireOp",EDGE,"E0.rect.right"),sQuery(id+"F0.wireOp",EDGE,"E1.1"),sQuery(id+"F0.wireOp",EDGE,"E1.2"),sQuery(id+"F0.wireOp",EDGE,"E3"),sQuery(id+"F0.wireOp",EDGE,"E4")])]}),"instanceName":"1"}),"instanceName":"1"});
            booleanBodies(context, id + "F20", {"operationType" : BooleanOperationType.UNION, "tools" : qUnion([Q0, Q1])});
        }
        {
            var Q0;
            Q0=makeQuery(id+"F20.opBoolean","MERGE",EDGE,{"derivedFrom":[makeQuery(id+"F1.opExtrude","SWEPT_EDGE",EDGE,{"disambiguationData":[OSD([sQuery(id+"F0.wireOp",EDGE,"E0.rect.bottom"),sQuery(id+"F0.wireOp",EDGE,"E4")])]}),makeQuery(id+"F18.opPattern","COPY",EDGE,{"derivedFrom":makeQuery(id+"F16.opPattern","COPY",EDGE,{"derivedFrom":makeQuery(id+"F1.opExtrude","SWEPT_EDGE",EDGE,{"disambiguationData":[OSD([sQuery(id+"F0.wireOp",EDGE,"E0.rect.right"),sQuery(id+"F0.wireOp",EDGE,"E3")])]}),"instanceName":"1"}),"instanceName":"1"})]});
            var Q1;
            Q1=makeQuery(id+"F1.opExtrude","SWEPT_EDGE",EDGE,{"disambiguationData":[OSD([sQuery(id+"F0.wireOp",EDGE,"E0.rect.bottom"),sQuery(id+"F0.wireOp",EDGE,"E0.rect.right")])]});
            var Q2;
            Q2=makeQuery(id+"F20.opBoolean","MERGE",EDGE,{"derivedFrom":[makeQuery(id+"F1.opExtrude","SWEPT_EDGE",EDGE,{"disambiguationData":[OSD([sQuery(id+"F0.wireOp",EDGE,"E0.rect.right"),sQuery(id+"F0.wireOp",EDGE,"E3")])]}),makeQuery(id+"F18.opPattern","COPY",EDGE,{"derivedFrom":makeQuery(id+"F16.opPattern","COPY",EDGE,{"derivedFrom":makeQuery(id+"F1.opExtrude","SWEPT_EDGE",EDGE,{"disambiguationData":[OSD([sQuery(id+"F0.wireOp",EDGE,"E0.rect.bottom"),sQuery(id+"F0.wireOp",EDGE,"E4")])]}),"instanceName":"1"}),"instanceName":"1"})]});
            var Q3;
            Q3=makeQuery(id+"F18.opPattern","COPY",EDGE,{"derivedFrom":makeQuery(id+"F16.opPattern","COPY",EDGE,{"derivedFrom":makeQuery(id+"F1.opExtrude","SWEPT_EDGE",EDGE,{"disambiguationData":[OSD([sQuery(id+"F0.wireOp",EDGE,"E0.rect.bottom"),sQuery(id+"F0.wireOp",EDGE,"E0.rect.right")])]}),"instanceName":"1"}),"instanceName":"1"});
            fillet(context, id + "F21", {"entities" : qUnion([Q0, Q1, Q2, Q3]), "radius" : 1 * mm, "tangentPropagation" : true, "allowEdgeOverflow" : false});
        }
        {
            var Q0;
            {var subQ0=sQuery(id+"F0.wireOp",EDGE,"E1.1");var subQ1=sQuery(id+"F0.wireOp",EDGE,"E1.2");var subQ2=makeQuery(id+"F11.opExtrude","SWEPT_FACE",FACE,{"disambiguationData":[OSD([sQuery(id+"F9.wireOp",EDGE,"E15.rect.bottom")])]});Q0=makeQuery(id+"F13.boolean.opBoolean","SPLIT",EDGE,{"disambiguationData":[TD([subQ2])],"derivedFrom":makeQuery(id+"F11.boolean.opBoolean","SPLIT",EDGE,{"disambiguationData":[TD([subQ2])],"derivedFrom":makeQuery(id+"F2.boolean.opBoolean","MERGE",EDGE,{"derivedFrom":[makeQuery(id+"F1.opExtrude","SWEPT_EDGE",EDGE,{"disambiguationData":[OSD([subQ0,subQ1])]}),makeQuery(id+"F2.opExtrude","SWEPT_EDGE",EDGE,{"disambiguationData":[OSD([subQ0,subQ1])]})]})})});}
            var Q1;
            {var subQ0=sQuery(id+"F0.wireOp",EDGE,"E1.1");var subQ1=sQuery(id+"F0.wireOp",EDGE,"E1.2");var subQ2=makeQuery(id+"F11.opExtrude","SWEPT_FACE",FACE,{"disambiguationData":[OSD([sQuery(id+"F9.wireOp",EDGE,"E20.trimOffspring")])]});Q1=makeQuery(id+"F13.boolean.opBoolean","SPLIT",EDGE,{"disambiguationData":[TD([subQ2])],"derivedFrom":makeQuery(id+"F11.boolean.opBoolean","SPLIT",EDGE,{"disambiguationData":[TD([makeQuery(id+"F11.opExtrude","SWEPT_FACE",FACE,{"disambiguationData":[OSD([sQuery(id+"F9.wireOp",EDGE,"E15.rect.bottom")])]})])],"derivedFrom":makeQuery(id+"F2.boolean.opBoolean","MERGE",EDGE,{"derivedFrom":[makeQuery(id+"F1.opExtrude","SWEPT_EDGE",EDGE,{"disambiguationData":[OSD([subQ0,subQ1])]}),makeQuery(id+"F2.opExtrude","SWEPT_EDGE",EDGE,{"disambiguationData":[OSD([subQ0,subQ1])]})]})})});}
            var Q2;
            {var subQ0=sQuery(id+"F0.wireOp",EDGE,"E1.1");var subQ1=sQuery(id+"F0.wireOp",EDGE,"E1.2");Q2=makeQuery(id+"F11.boolean.opBoolean","SPLIT",EDGE,{"disambiguationData":[TD([makeQuery(id+"F11.opExtrude","SWEPT_FACE",FACE,{"disambiguationData":[OSD([sQuery(id+"F9.wireOp",EDGE,"E17.0")])]})])],"derivedFrom":makeQuery(id+"F2.boolean.opBoolean","MERGE",EDGE,{"derivedFrom":[makeQuery(id+"F1.opExtrude","SWEPT_EDGE",EDGE,{"disambiguationData":[OSD([subQ0,subQ1])]}),makeQuery(id+"F2.opExtrude","SWEPT_EDGE",EDGE,{"disambiguationData":[OSD([subQ0,subQ1])]})]})});}
            var Q3;
            {var subQ0=sQuery(id+"F0.wireOp",EDGE,"E1.2");var subQ1=sQuery(id+"F0.wireOp",EDGE,"E3");var subQ2=makeQuery(id+"F11.opExtrude","SWEPT_FACE",FACE,{"disambiguationData":[OSD([sQuery(id+"F9.wireOp",EDGE,"E15.rect.bottom")])]});var subQ3=sQuery(id+"F0.wireOp",EDGE,"E1.1");var subQ4=sQuery(id+"F0.wireOp",EDGE,"E4");Q3=makeQuery(id+"F20.opBoolean","MERGE",EDGE,{"derivedFrom":[makeQuery(id+"F13.boolean.opBoolean","SPLIT",EDGE,{"disambiguationData":[TD([subQ2])],"derivedFrom":makeQuery(id+"F2.boolean.opBoolean","MERGE",EDGE,{"derivedFrom":[makeQuery(id+"F1.opExtrude","SWEPT_EDGE",EDGE,{"disambiguationData":[OSD([subQ0,subQ1])]}),makeQuery(id+"F2.opExtrude","SWEPT_EDGE",EDGE,{"disambiguationData":[OSD([subQ0,subQ1])]})]})}),makeQuery(id+"F18.opPattern","COPY",EDGE,{"derivedFrom":makeQuery(id+"F16.opPattern","COPY",EDGE,{"derivedFrom":makeQuery(id+"F11.boolean.opBoolean","SPLIT",EDGE,{"disambiguationData":[TD([subQ2])],"derivedFrom":makeQuery(id+"F2.boolean.opBoolean","MERGE",EDGE,{"derivedFrom":[makeQuery(id+"F1.opExtrude","SWEPT_EDGE",EDGE,{"disambiguationData":[OSD([subQ3,subQ4])]}),makeQuery(id+"F2.opExtrude","SWEPT_EDGE",EDGE,{"disambiguationData":[OSD([subQ3,subQ4])]})]})}),"instanceName":"1"}),"instanceName":"1"})]});}
            var Q4;
            {var subQ0=sQuery(id+"F0.wireOp",EDGE,"E1.2");var subQ1=sQuery(id+"F0.wireOp",EDGE,"E3");var subQ2=sQuery(id+"F0.wireOp",EDGE,"E1.1");var subQ3=sQuery(id+"F0.wireOp",EDGE,"E4");Q4=makeQuery(id+"F20.opBoolean","MERGE",EDGE,{"derivedFrom":[makeQuery(id+"F13.boolean.opBoolean","SPLIT",EDGE,{"disambiguationData":[TD([makeQuery(id+"F11.opExtrude","SWEPT_FACE",FACE,{"disambiguationData":[OSD([sQuery(id+"F9.wireOp",EDGE,"E17.0")])]})])],"derivedFrom":makeQuery(id+"F2.boolean.opBoolean","MERGE",EDGE,{"derivedFrom":[makeQuery(id+"F1.opExtrude","SWEPT_EDGE",EDGE,{"disambiguationData":[OSD([subQ0,subQ1])]}),makeQuery(id+"F2.opExtrude","SWEPT_EDGE",EDGE,{"disambiguationData":[OSD([subQ0,subQ1])]})]})}),makeQuery(id+"F18.opPattern","COPY",EDGE,{"derivedFrom":makeQuery(id+"F16.opPattern","COPY",EDGE,{"derivedFrom":makeQuery(id+"F11.boolean.opBoolean","SPLIT",EDGE,{"disambiguationData":[TD([makeQuery(id+"F11.opExtrude","SWEPT_FACE",FACE,{"disambiguationData":[OSD([sQuery(id+"F9.wireOp",EDGE,"E15.rect.bottom")])]})])],"derivedFrom":makeQuery(id+"F2.boolean.opBoolean","MERGE",EDGE,{"derivedFrom":[makeQuery(id+"F1.opExtrude","SWEPT_EDGE",EDGE,{"disambiguationData":[OSD([subQ2,subQ3])]}),makeQuery(id+"F2.opExtrude","SWEPT_EDGE",EDGE,{"disambiguationData":[OSD([subQ2,subQ3])]})]})}),"instanceName":"1"}),"instanceName":"1"})]});}
            var Q5;
            {var subQ0=sQuery(id+"F0.wireOp",EDGE,"E1.2");var subQ1=sQuery(id+"F0.wireOp",EDGE,"E3");var subQ2=makeQuery(id+"F11.opExtrude","SWEPT_FACE",FACE,{"disambiguationData":[OSD([sQuery(id+"F9.wireOp",EDGE,"E17.0")])]});var subQ3=sQuery(id+"F0.wireOp",EDGE,"E1.1");var subQ4=sQuery(id+"F0.wireOp",EDGE,"E4");Q5=makeQuery(id+"F20.opBoolean","MERGE",EDGE,{"derivedFrom":[makeQuery(id+"F13.boolean.opBoolean","SPLIT",EDGE,{"disambiguationData":[TD([subQ2])],"derivedFrom":makeQuery(id+"F2.boolean.opBoolean","MERGE",EDGE,{"derivedFrom":[makeQuery(id+"F1.opExtrude","SWEPT_EDGE",EDGE,{"disambiguationData":[OSD([subQ0,subQ1])]}),makeQuery(id+"F2.opExtrude","SWEPT_EDGE",EDGE,{"disambiguationData":[OSD([subQ0,subQ1])]})]})}),makeQuery(id+"F18.opPattern","COPY",EDGE,{"derivedFrom":makeQuery(id+"F16.opPattern","COPY",EDGE,{"derivedFrom":makeQuery(id+"F11.boolean.opBoolean","SPLIT",EDGE,{"disambiguationData":[TD([makeQuery(id+"F11.opExtrude","SWEPT_FACE",FACE,{"disambiguationData":[OSD([sQuery(id+"F9.wireOp",EDGE,"E16.rect.top")])]})])],"derivedFrom":makeQuery(id+"F2.boolean.opBoolean","MERGE",EDGE,{"derivedFrom":[makeQuery(id+"F1.opExtrude","SWEPT_EDGE",EDGE,{"disambiguationData":[OSD([subQ3,subQ4])]}),makeQuery(id+"F2.opExtrude","SWEPT_EDGE",EDGE,{"disambiguationData":[OSD([subQ3,subQ4])]})]})}),"instanceName":"1"}),"instanceName":"1"})]});}
            var Q6;
            {var subQ0=sQuery(id+"F0.wireOp",EDGE,"E1.1");var subQ1=sQuery(id+"F0.wireOp",EDGE,"E1.2");Q6=makeQuery(id+"F18.opPattern","COPY",EDGE,{"derivedFrom":makeQuery(id+"F16.opPattern","COPY",EDGE,{"derivedFrom":makeQuery(id+"F11.boolean.opBoolean","SPLIT",EDGE,{"disambiguationData":[TD([makeQuery(id+"F11.opExtrude","SWEPT_FACE",FACE,{"disambiguationData":[OSD([sQuery(id+"F9.wireOp",EDGE,"E17.0")])]})])],"derivedFrom":makeQuery(id+"F2.boolean.opBoolean","MERGE",EDGE,{"derivedFrom":[makeQuery(id+"F1.opExtrude","SWEPT_EDGE",EDGE,{"disambiguationData":[OSD([subQ0,subQ1])]}),makeQuery(id+"F2.opExtrude","SWEPT_EDGE",EDGE,{"disambiguationData":[OSD([subQ0,subQ1])]})]})}),"instanceName":"1"}),"instanceName":"1"});}
            var Q7;
            {var subQ0=sQuery(id+"F0.wireOp",EDGE,"E1.1");var subQ1=sQuery(id+"F0.wireOp",EDGE,"E1.2");var subQ2=makeQuery(id+"F11.opExtrude","SWEPT_FACE",FACE,{"disambiguationData":[OSD([sQuery(id+"F9.wireOp",EDGE,"E20.trimOffspring")])]});Q7=makeQuery(id+"F18.opPattern","COPY",EDGE,{"derivedFrom":makeQuery(id+"F16.opPattern","COPY",EDGE,{"derivedFrom":makeQuery(id+"F13.boolean.opBoolean","SPLIT",EDGE,{"disambiguationData":[TD([subQ2])],"derivedFrom":makeQuery(id+"F11.boolean.opBoolean","SPLIT",EDGE,{"disambiguationData":[TD([makeQuery(id+"F11.opExtrude","SWEPT_FACE",FACE,{"disambiguationData":[OSD([sQuery(id+"F9.wireOp",EDGE,"E15.rect.bottom")])]})])],"derivedFrom":makeQuery(id+"F2.boolean.opBoolean","MERGE",EDGE,{"derivedFrom":[makeQuery(id+"F1.opExtrude","SWEPT_EDGE",EDGE,{"disambiguationData":[OSD([subQ0,subQ1])]}),makeQuery(id+"F2.opExtrude","SWEPT_EDGE",EDGE,{"disambiguationData":[OSD([subQ0,subQ1])]})]})})}),"instanceName":"1"}),"instanceName":"1"});}
            var Q8;
            {var subQ0=sQuery(id+"F0.wireOp",EDGE,"E1.1");var subQ1=sQuery(id+"F0.wireOp",EDGE,"E1.2");var subQ2=makeQuery(id+"F11.opExtrude","SWEPT_FACE",FACE,{"disambiguationData":[OSD([sQuery(id+"F9.wireOp",EDGE,"E15.rect.bottom")])]});Q8=makeQuery(id+"F18.opPattern","COPY",EDGE,{"derivedFrom":makeQuery(id+"F16.opPattern","COPY",EDGE,{"derivedFrom":makeQuery(id+"F13.boolean.opBoolean","SPLIT",EDGE,{"disambiguationData":[TD([subQ2])],"derivedFrom":makeQuery(id+"F11.boolean.opBoolean","SPLIT",EDGE,{"disambiguationData":[TD([subQ2])],"derivedFrom":makeQuery(id+"F2.boolean.opBoolean","MERGE",EDGE,{"derivedFrom":[makeQuery(id+"F1.opExtrude","SWEPT_EDGE",EDGE,{"disambiguationData":[OSD([subQ0,subQ1])]}),makeQuery(id+"F2.opExtrude","SWEPT_EDGE",EDGE,{"disambiguationData":[OSD([subQ0,subQ1])]})]})})}),"instanceName":"1"}),"instanceName":"1"});}
            var Q9;
            {var subQ0=sQuery(id+"F0.wireOp",EDGE,"E1.1");var subQ1=sQuery(id+"F0.wireOp",EDGE,"E4");var subQ2=makeQuery(id+"F11.opExtrude","SWEPT_FACE",FACE,{"disambiguationData":[OSD([sQuery(id+"F9.wireOp",EDGE,"E15.rect.bottom")])]});var subQ3=sQuery(id+"F0.wireOp",EDGE,"E1.2");var subQ4=sQuery(id+"F0.wireOp",EDGE,"E3");Q9=makeQuery(id+"F20.opBoolean","MERGE",EDGE,{"derivedFrom":[makeQuery(id+"F11.boolean.opBoolean","SPLIT",EDGE,{"disambiguationData":[TD([subQ2])],"derivedFrom":makeQuery(id+"F2.boolean.opBoolean","MERGE",EDGE,{"derivedFrom":[makeQuery(id+"F1.opExtrude","SWEPT_EDGE",EDGE,{"disambiguationData":[OSD([subQ0,subQ1])]}),makeQuery(id+"F2.opExtrude","SWEPT_EDGE",EDGE,{"disambiguationData":[OSD([subQ0,subQ1])]})]})}),makeQuery(id+"F18.opPattern","COPY",EDGE,{"derivedFrom":makeQuery(id+"F16.opPattern","COPY",EDGE,{"derivedFrom":makeQuery(id+"F13.boolean.opBoolean","SPLIT",EDGE,{"disambiguationData":[TD([subQ2])],"derivedFrom":makeQuery(id+"F2.boolean.opBoolean","MERGE",EDGE,{"derivedFrom":[makeQuery(id+"F1.opExtrude","SWEPT_EDGE",EDGE,{"disambiguationData":[OSD([subQ3,subQ4])]}),makeQuery(id+"F2.opExtrude","SWEPT_EDGE",EDGE,{"disambiguationData":[OSD([subQ3,subQ4])]})]})}),"instanceName":"1"}),"instanceName":"1"})]});}
            var Q10;
            {var subQ0=sQuery(id+"F0.wireOp",EDGE,"E1.1");var subQ1=sQuery(id+"F0.wireOp",EDGE,"E4");var subQ2=sQuery(id+"F0.wireOp",EDGE,"E1.2");var subQ3=sQuery(id+"F0.wireOp",EDGE,"E3");Q10=makeQuery(id+"F20.opBoolean","MERGE",EDGE,{"derivedFrom":[makeQuery(id+"F11.boolean.opBoolean","SPLIT",EDGE,{"disambiguationData":[TD([makeQuery(id+"F11.opExtrude","SWEPT_FACE",FACE,{"disambiguationData":[OSD([sQuery(id+"F9.wireOp",EDGE,"E15.rect.bottom")])]})])],"derivedFrom":makeQuery(id+"F2.boolean.opBoolean","MERGE",EDGE,{"derivedFrom":[makeQuery(id+"F1.opExtrude","SWEPT_EDGE",EDGE,{"disambiguationData":[OSD([subQ0,subQ1])]}),makeQuery(id+"F2.opExtrude","SWEPT_EDGE",EDGE,{"disambiguationData":[OSD([subQ0,subQ1])]})]})}),makeQuery(id+"F18.opPattern","COPY",EDGE,{"derivedFrom":makeQuery(id+"F16.opPattern","COPY",EDGE,{"derivedFrom":makeQuery(id+"F13.boolean.opBoolean","SPLIT",EDGE,{"disambiguationData":[TD([makeQuery(id+"F11.opExtrude","SWEPT_FACE",FACE,{"disambiguationData":[OSD([sQuery(id+"F9.wireOp",EDGE,"E17.0")])]})])],"derivedFrom":makeQuery(id+"F2.boolean.opBoolean","MERGE",EDGE,{"derivedFrom":[makeQuery(id+"F1.opExtrude","SWEPT_EDGE",EDGE,{"disambiguationData":[OSD([subQ2,subQ3])]}),makeQuery(id+"F2.opExtrude","SWEPT_EDGE",EDGE,{"disambiguationData":[OSD([subQ2,subQ3])]})]})}),"instanceName":"1"}),"instanceName":"1"})]});}
            var Q11;
            {var subQ0=sQuery(id+"F0.wireOp",EDGE,"E1.1");var subQ1=sQuery(id+"F0.wireOp",EDGE,"E4");var subQ2=makeQuery(id+"F11.opExtrude","SWEPT_FACE",FACE,{"disambiguationData":[OSD([sQuery(id+"F9.wireOp",EDGE,"E17.0")])]});var subQ3=sQuery(id+"F0.wireOp",EDGE,"E1.2");var subQ4=sQuery(id+"F0.wireOp",EDGE,"E3");Q11=makeQuery(id+"F20.opBoolean","MERGE",EDGE,{"derivedFrom":[makeQuery(id+"F11.boolean.opBoolean","SPLIT",EDGE,{"disambiguationData":[TD([makeQuery(id+"F11.opExtrude","SWEPT_FACE",FACE,{"disambiguationData":[OSD([sQuery(id+"F9.wireOp",EDGE,"E16.rect.top")])]})])],"derivedFrom":makeQuery(id+"F2.boolean.opBoolean","MERGE",EDGE,{"derivedFrom":[makeQuery(id+"F1.opExtrude","SWEPT_EDGE",EDGE,{"disambiguationData":[OSD([subQ0,subQ1])]}),makeQuery(id+"F2.opExtrude","SWEPT_EDGE",EDGE,{"disambiguationData":[OSD([subQ0,subQ1])]})]})}),makeQuery(id+"F18.opPattern","COPY",EDGE,{"derivedFrom":makeQuery(id+"F16.opPattern","COPY",EDGE,{"derivedFrom":makeQuery(id+"F13.boolean.opBoolean","SPLIT",EDGE,{"disambiguationData":[TD([subQ2])],"derivedFrom":makeQuery(id+"F2.boolean.opBoolean","MERGE",EDGE,{"derivedFrom":[makeQuery(id+"F1.opExtrude","SWEPT_EDGE",EDGE,{"disambiguationData":[OSD([subQ3,subQ4])]}),makeQuery(id+"F2.opExtrude","SWEPT_EDGE",EDGE,{"disambiguationData":[OSD([subQ3,subQ4])]})]})}),"instanceName":"1"}),"instanceName":"1"})]});}
            var Q12;
            Q12=makeQuery(id+"F13.opExtrude","CAP_EDGE",EDGE,{"disambiguationData":[OSD([sQuery(id+"F10.wireOp",EDGE,"E28.rect.right")])],"isStart":false});
            var Q13;
            Q13=makeQuery(id+"F18.opPattern","COPY",EDGE,{"derivedFrom":makeQuery(id+"F16.opPattern","COPY",EDGE,{"derivedFrom":makeQuery(id+"F11.opExtrude","CAP_EDGE",EDGE,{"disambiguationData":[OSD([sQuery(id+"F9.wireOp",EDGE,"E16.rect.left")])],"isStart":false}),"instanceName":"1"}),"instanceName":"1"});
            var Q14;
            Q14=makeQuery(id+"F18.opPattern","COPY",EDGE,{"derivedFrom":makeQuery(id+"F16.opPattern","COPY",EDGE,{"derivedFrom":makeQuery(id+"F13.opExtrude","CAP_EDGE",EDGE,{"disambiguationData":[OSD([sQuery(id+"F10.wireOp",EDGE,"E28.rect.left")])],"isStart":false}),"instanceName":"1"}),"instanceName":"1"});
            var Q15;
            Q15=makeQuery(id+"F18.opPattern","COPY",EDGE,{"derivedFrom":makeQuery(id+"F16.opPattern","COPY",EDGE,{"derivedFrom":makeQuery(id+"F11.opExtrude","CAP_EDGE",EDGE,{"disambiguationData":[OSD([sQuery(id+"F9.wireOp",EDGE,"E16.rect.right")])],"isStart":false}),"instanceName":"1"}),"instanceName":"1"});
            var Q16;
            Q16=makeQuery(id+"F18.opPattern","COPY",EDGE,{"derivedFrom":makeQuery(id+"F16.opPattern","COPY",EDGE,{"derivedFrom":makeQuery(id+"F13.opExtrude","CAP_EDGE",EDGE,{"disambiguationData":[OSD([sQuery(id+"F10.wireOp",EDGE,"E28.rect.right")])],"isStart":false}),"instanceName":"1"}),"instanceName":"1"});
            var Q17;
            Q17=makeQuery(id+"F11.opExtrude","CAP_EDGE",EDGE,{"disambiguationData":[OSD([sQuery(id+"F9.wireOp",EDGE,"E16.rect.left")])],"isStart":false});
            var Q18;
            Q18=makeQuery(id+"F11.opExtrude","CAP_EDGE",EDGE,{"disambiguationData":[OSD([sQuery(id+"F9.wireOp",EDGE,"E16.rect.right")])],"isStart":false});
            var Q19;
            Q19=makeQuery(id+"F13.opExtrude","CAP_EDGE",EDGE,{"disambiguationData":[OSD([sQuery(id+"F10.wireOp",EDGE,"E28.rect.left")])],"isStart":false});
            var Q20;
            Q20=makeQuery(id+"F18.opPattern","COPY",EDGE,{"derivedFrom":makeQuery(id+"F16.opPattern","COPY",EDGE,{"derivedFrom":makeQuery(id+"F11.opExtrude","CAP_EDGE",EDGE,{"disambiguationData":[OSD([sQuery(id+"F9.wireOp",EDGE,"E15.rect.bottom")])],"isStart":false}),"instanceName":"1"}),"instanceName":"1"});
            var Q21;
            Q21=makeQuery(id+"F13.opExtrude","CAP_EDGE",EDGE,{"disambiguationData":[OSD([sQuery(id+"F10.wireOp",EDGE,"E27.0")])],"isStart":false});
            var Q22;
            Q22=makeQuery(id+"F11.opExtrude","CAP_EDGE",EDGE,{"disambiguationData":[OSD([sQuery(id+"F9.wireOp",EDGE,"E15.rect.bottom")])],"isStart":false});
            var Q23;
            Q23=makeQuery(id+"F18.opPattern","COPY",EDGE,{"derivedFrom":makeQuery(id+"F16.opPattern","COPY",EDGE,{"derivedFrom":makeQuery(id+"F13.opExtrude","CAP_EDGE",EDGE,{"disambiguationData":[OSD([sQuery(id+"F10.wireOp",EDGE,"E27.0")])],"isStart":false}),"instanceName":"1"}),"instanceName":"1"});
            fillet(context, id + "F22", {"entities" : qUnion([Q0, Q1, Q2, Q3, Q4, Q5, Q6, Q7, Q8, Q9, Q10, Q11, Q12, Q13, Q14, Q15, Q16, Q17, Q18, Q19, Q20, Q21, Q22, Q23]), "radius" : 4 * mm, "tangentPropagation" : true, "allowEdgeOverflow" : false});
        }
        {
            var Q0;
            Q0=makeQuery(id+"F15.imprint","IMPRINT",FACE,{"disambiguationData":[TD([[makeQuery(id+"F15.imprint","IMPRINT",EDGE,{"derivedFrom":sQuery(id+"F15.wireOp",EDGE,"E121.18")}),-1.0]])]});
            var Q1;
            Q1=makeQuery(id+"F15.imprint","IMPRINT",FACE,{"disambiguationData":[TD([[makeQuery(id+"F15.imprint","IMPRINT",EDGE,{"derivedFrom":sQuery(id+"F15.wireOp",EDGE,"E121.0")}),-1.0]])]});
            var Q2;
            Q2=makeQuery(id+"F15.imprint","IMPRINT",FACE,{"disambiguationData":[TD([[makeQuery(id+"F15.imprint","IMPRINT",EDGE,{"derivedFrom":sQuery(id+"F15.wireOp",EDGE,"E121.10")}),-1.0]])]});
            var Q3;
            Q3=makeQuery(id+"F15.imprint","IMPRINT",FACE,{"disambiguationData":[TD([[makeQuery(id+"F15.imprint","IMPRINT",EDGE,{"derivedFrom":sQuery(id+"F15.wireOp",EDGE,"E121.43")}),-1.0]])]});
            extrude(context, id + "F23", {"entities" : qUnion([Q0, Q1, Q2, Q3]), "operationType" : NewBodyOperationType.ADD, "depth" : 20 * mm});
        }
        {
            var Q0;
            Q0=makeQuery(id+"F23.opExtrude","CAP_FACE",FACE,{"disambiguationData":[OSD([sQuery(id+"F15.wireOp",EDGE,"E121.10"),sQuery(id+"F15.wireOp",EDGE,"E121.11"),sQuery(id+"F15.wireOp",EDGE,"E121.12"),sQuery(id+"F15.wireOp",EDGE,"E121.13"),sQuery(id+"F15.wireOp",EDGE,"E121.14"),sQuery(id+"F15.wireOp",EDGE,"E121.15"),sQuery(id+"F15.wireOp",EDGE,"E121.16"),sQuery(id+"F15.wireOp",EDGE,"E121.17"),sQuery(id+"F15.wireOp",EDGE,"E121.59"),sQuery(id+"F15.wireOp",EDGE,"E121.60"),sQuery(id+"F15.wireOp",EDGE,"E121.61"),sQuery(id+"F15.wireOp",EDGE,"E121.62"),sQuery(id+"F15.wireOp",EDGE,"E121.63"),sQuery(id+"F15.wireOp",EDGE,"E125")])],"isStart":false});
            var Q1;
            Q1=makeQuery(id+"F23.opExtrude","CAP_FACE",FACE,{"disambiguationData":[OSD([sQuery(id+"F15.wireOp",EDGE,"E121.18"),sQuery(id+"F15.wireOp",EDGE,"E121.19"),sQuery(id+"F15.wireOp",EDGE,"E121.20"),sQuery(id+"F15.wireOp",EDGE,"E121.21"),sQuery(id+"F15.wireOp",EDGE,"E121.22"),sQuery(id+"F15.wireOp",EDGE,"E121.23"),sQuery(id+"F15.wireOp",EDGE,"E121.24"),sQuery(id+"F15.wireOp",EDGE,"E121.25"),sQuery(id+"F15.wireOp",EDGE,"E121.26"),sQuery(id+"F15.wireOp",EDGE,"E121.27"),sQuery(id+"F15.wireOp",EDGE,"E121.28"),sQuery(id+"F15.wireOp",EDGE,"E121.29"),sQuery(id+"F15.wireOp",EDGE,"E121.39"),sQuery(id+"F15.wireOp",EDGE,"E123")])],"isStart":false});
            extrude(context, id + "F24", {"entities" : qUnion([Q0, Q1]), "operationType" : NewBodyOperationType.ADD, "depth" : 20 * mm});
        }
        {
            var Q0;
            Q0=makeQuery(id+"F24.opExtrude","SWEPT_FACE",FACE,{"disambiguationData":[OSD([sQuery(id+"F0.wireOp",EDGE,"E0.rect.right"),sQuery(id+"F15.wireOp",EDGE,"E121.10"),sQuery(id+"F15.wireOp",EDGE,"E121.11"),sQuery(id+"F15.wireOp",EDGE,"E121.12"),sQuery(id+"F15.wireOp",EDGE,"E121.13"),sQuery(id+"F15.wireOp",EDGE,"E121.14"),sQuery(id+"F15.wireOp",EDGE,"E121.15"),sQuery(id+"F15.wireOp",EDGE,"E121.16"),sQuery(id+"F15.wireOp",EDGE,"E121.17"),sQuery(id+"F15.wireOp",EDGE,"E121.59"),sQuery(id+"F15.wireOp",EDGE,"E121.60"),sQuery(id+"F15.wireOp",EDGE,"E121.61"),sQuery(id+"F15.wireOp",EDGE,"E121.62"),sQuery(id+"F15.wireOp",EDGE,"E121.63"),sQuery(id+"F15.wireOp",EDGE,"E125")])]});
            extrude(context, id + "F25", {"entities" : qUnion([Q0]), "operationType" : NewBodyOperationType.REMOVE, "endBound" : BoundingType.THROUGH_ALL, "oppositeDirection" : true, "depth" : 25 * mm});
        }
        {
            var Q0;
            Q0=makeQuery(id+"F23.opExtrude","SWEPT_FACE",FACE,{"disambiguationData":[OSD([sQuery(id+"F15.wireOp",EDGE,"E122")])]});
            extrude(context, id + "F26", {"entities" : qUnion([Q0]), "operationType" : NewBodyOperationType.REMOVE, "endBound" : BoundingType.THROUGH_ALL, "oppositeDirection" : true, "depth" : 25 * mm});
        }
    });
